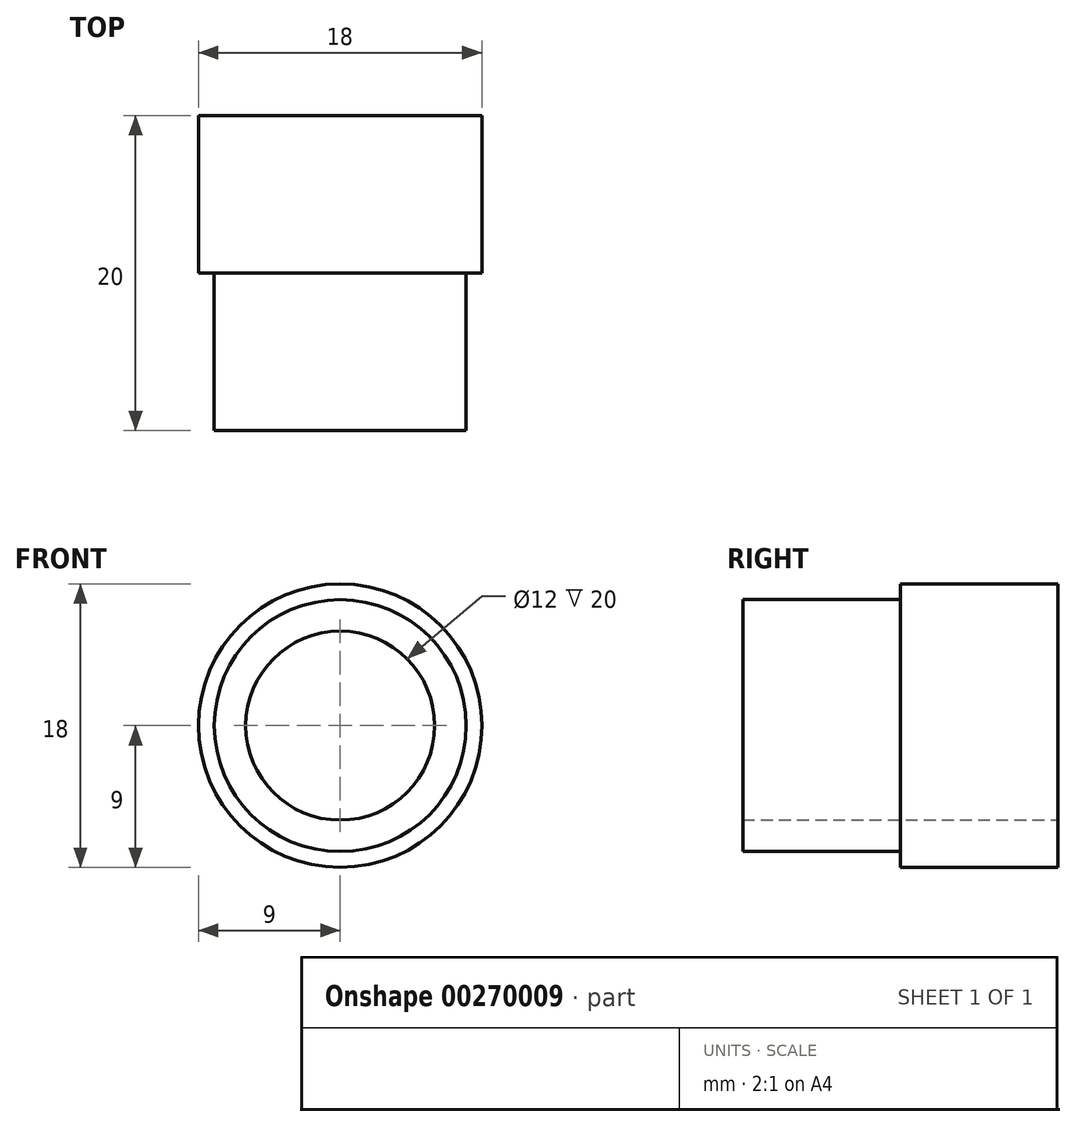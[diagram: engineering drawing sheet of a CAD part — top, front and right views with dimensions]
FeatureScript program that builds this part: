
annotation { "Feature Type Name" : "Feature", "Feature Type Description" : "" }
export const myFeature = defineFeature(function(context is Context, id is Id, definition is map)
    precondition{}
    {
        {
            var Q0;
            Q0=qCreatedBy(makeId("Front.planeOp"),FACE);
            var sketch = newSketch(context, id + "F0", { "sketchPlane" : qUnion([Q0])});
            skCircle(sketch, "E0", {"center": v(0, 0) * mm, "radius": 6 * mm});
            skCircle(sketch, "E1", {"center": v(0, 0) * mm, "radius": 8 * mm});
            skSolve(sketch);
        }
        {
            var Q0;
            Q0=makeQuery(id+"F0.imprint","IMPRINT",FACE,{"disambiguationData":[TD([[makeQuery(id+"F0.imprint","IMPRINT",EDGE,{"derivedFrom":sQuery(id+"F0.wireOp",EDGE,"E0")}),-1.0]])]});
            extrude(context, id + "F1", {"entities" : qUnion([Q0]), "depth" : 10 * mm});
        }
        {
            var Q0;
            Q0=makeQuery(id+"F1.opExtrude","CAP_FACE",FACE,{"disambiguationData":[OSD([sQuery(id+"F0.wireOp",EDGE,"E0"),sQuery(id+"F0.wireOp",EDGE,"E1")])],"isStart":true});
            var sketch = newSketch(context, id + "F2", { "sketchPlane" : qUnion([Q0])});
            skCircle(sketch, "E2", {"center": v(0, 0) * mm, "radius": 6 * mm});
            skCircle(sketch, "E3", {"center": v(0, 0) * mm, "radius": 9 * mm});
            skSolve(sketch);
        }
        {
            var Q0;
            Q0 = qSketchRegion(id + "F2", true);
            extrude(context, id + "F3", {"entities" : qUnion([Q0]), "operationType" : NewBodyOperationType.ADD, "depth" : 10 * mm});
        }
    });
